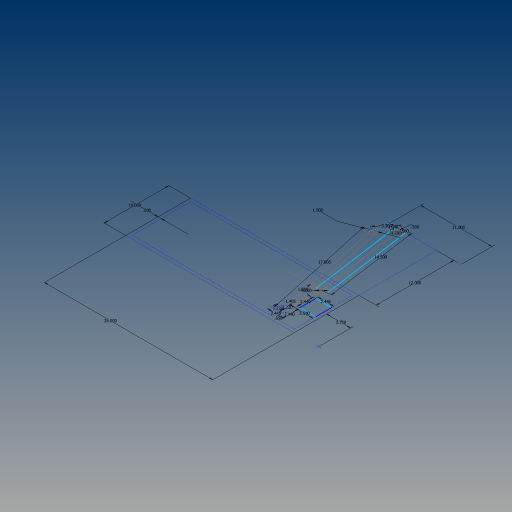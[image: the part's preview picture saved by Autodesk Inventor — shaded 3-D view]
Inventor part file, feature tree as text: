
AUTODESK INVENTOR PART (.ipt)
format: ipt  version: 2024.3 (Build 283343000, 343)  size: 120,832 bytes
history: native  units: in
note: dims shown in document units (in); Inventor stores cm internally (conversion verified against a paired STEP export)
features: sketch x1
ambient origin geometry x8: Origin, YZ Plane, XZ Plane, XY Plane, X Axis, Y Axis, Z Axis, Center Point
feature tree (1):
  sketch  "Sketch1"  dims[d0=26.0in d1=10.0in d2=0.5in d3=3.75in d4=12.0in d5=11.0in d8=1.22in d9=1.22in d10=2.44in d11=2.44in d12=1.2in d15=3.5in d20=3.3in d24=1.0in d31=0.5563in d34=17.8in d35=14.5in d38=1.405in d39=1.5in d41=1.5in d42=0.5in d43=0.5in d44=2.44in d45=2.44in d46=90.0deg]
